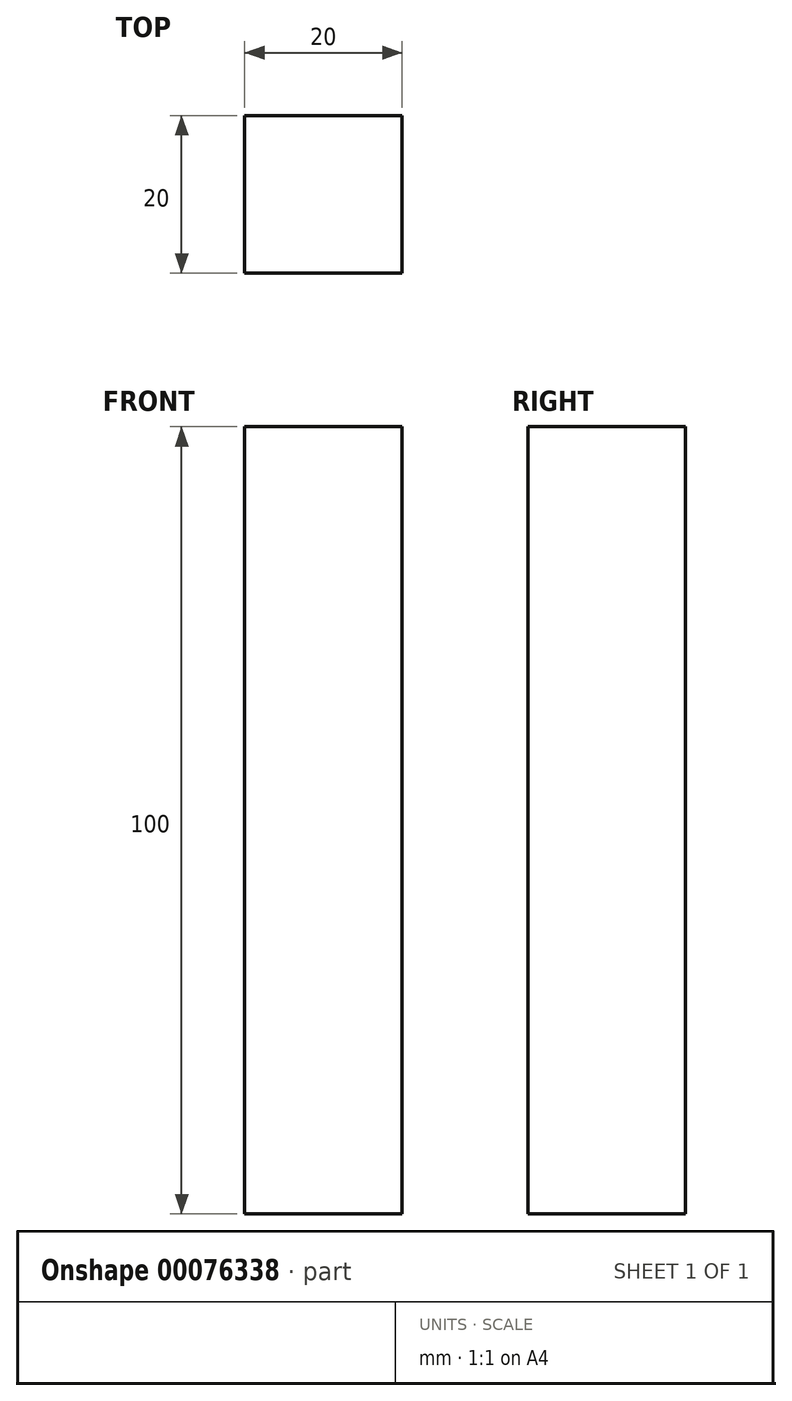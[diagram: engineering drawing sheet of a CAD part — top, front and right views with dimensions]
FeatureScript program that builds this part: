
annotation { "Feature Type Name" : "Feature", "Feature Type Description" : "" }
export const myFeature = defineFeature(function(context is Context, id is Id, definition is map)
    precondition{}
    {
        {
            var Q0;
            Q0=qCreatedBy(makeId("Top.planeOp"),FACE);
            var sketch = newSketch(context, id + "F0", { "sketchPlane" : qUnion([Q0])});
            skLineSegment(sketch, "E0.bottom", {"start": v(0, 0) * mm, "end": v(-20, 0) * mm});
            skLineSegment(sketch, "E0.top", {"start": v(0, 20) * mm, "end": v(-20, 20) * mm});
            skLineSegment(sketch, "E0.left", {"start": v(0, 0) * mm, "end": v(0, 20) * mm});
            skLineSegment(sketch, "E0.right", {"start": v(-20, 0) * mm, "end": v(-20, 20) * mm});
            skSolve(sketch);
        }
        {
            var Q0;
            Q0 = qSketchRegion(id + "F0", true);
            extrude(context, id + "F1", {"entities" : qUnion([Q0]), "depth" : 100 * mm});
        }
    });
